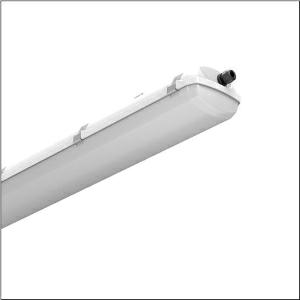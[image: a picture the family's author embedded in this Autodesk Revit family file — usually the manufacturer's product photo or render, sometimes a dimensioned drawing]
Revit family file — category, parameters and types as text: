
# Revit family: monsun_r__ex_51fxb27l680a_8a22
name_source: partatom
category: Lighting Fixtures
units: mm (PartAtom-declared; Revit-internal decimal feet)

## family parameters
Cut with Voids When Loaded = No
Host = Face
Light Source = No
Part Type = Normal
Room Calculation Point = No
Round Connector Dimension = Use Diameter
Shared = No

## types (1)
- Monsun® Ex (1 x LED, 8720 lm, 58.4 W, 6500K)
    Apparent Load = 58 VA
    CIE Flux Codes = 43 72 91 92 100
    Color Rendering = 80
    Color Temperature = 6500K
    Default Elevation = 1800 mm
    Description = Monsun® Ex, damp-proof luminaire, primary optical cover: cover, of PC, UV-stabilised, opal, light emission: direct distribution, primary light characteristic: symmetric, installation type: surface-mounted, LED, rated luminous flux: 8.720lm, luminous efficacy: 149lm/W, light colour: 865, colour temperature: 6500K, control gear: ECG, with terminal, 3-pole, max. 2.5mm², through-wiring: 5x 2.5mm², mains connection: 220..240V, AC, 50/60Hz, rated input power: 58W, housing, of PC, light grey (RAL 7035), incl. blind plug, incl. 1x Ex cable gland M20 for cable diameter 7..12mm with sealing, length: 1.280mm, width: 155mm, height: 105mm, clip for enclosure, of stainless steel, protection rating (complete): IP66, insulation class (complete): insulation class I (protective earthing), certification: CE, explosion class: zone2,22 II 3G Ex nR IIC T6 GC, II 3D Ex tc IIIC T80°C Dc, impact resistance: IK10, permissible operating ambient temperature: -20..+40°C, LABS conformity tested according to VDMA 24364:2018-05, contact your sales advisor before using the luminaires in applications with unclear chemical exposure, large temperature fluctuations or condensation-forming humidity, packaging unit: 1 piece
    Height = 105 mm
    Lamp = 1 x LED
    Lamp Light Flux = 8720 lm
    Lamp Power = 58.4 W
    Lamp count = 1
    Length = 1280 mm
    Luminous efficacy = 149 lm/W
    Manufacturer = Siteco
    ModVariant = No
    Model = 51FXB27L680A
    Mounting Place = Ceiling
    Mounting Type = Surface mounted
    Number of Poles = 1
    OnlyDefault = Yes
    Power Factor = 1
    Product Name = Monsun® Ex
    Product group = damp-proof luminaire
    ProductGroupID = 301
    Protection Class = Protection class I
    Protection Degree = IP 66
    RLX_Detail_Level = 1
    RLX_Emergency_Light_Flux = 0 lm
    RLX_Emergency_Type = 0
    RLX_Emergency_Type_DB = No
    RlxData = <blob elided: 41529 chars, md5=925ae83b>
    Socket = socket
    Standby Power = 0 W
    System Light Flux = 8720 lm
    System Power = 58 W
    Type Comments = Product without accessories
    Type Image = l_1258882.jpg
    URL = http://relux.com
    VarID = ---
    Voltage = 0 V
    Weight = 0.00 kg
    Width = 155 mm

## geometry (parser evidence)
native form markers: Blend x4, Sweep x12
no freeform markers — native parametric forms only
